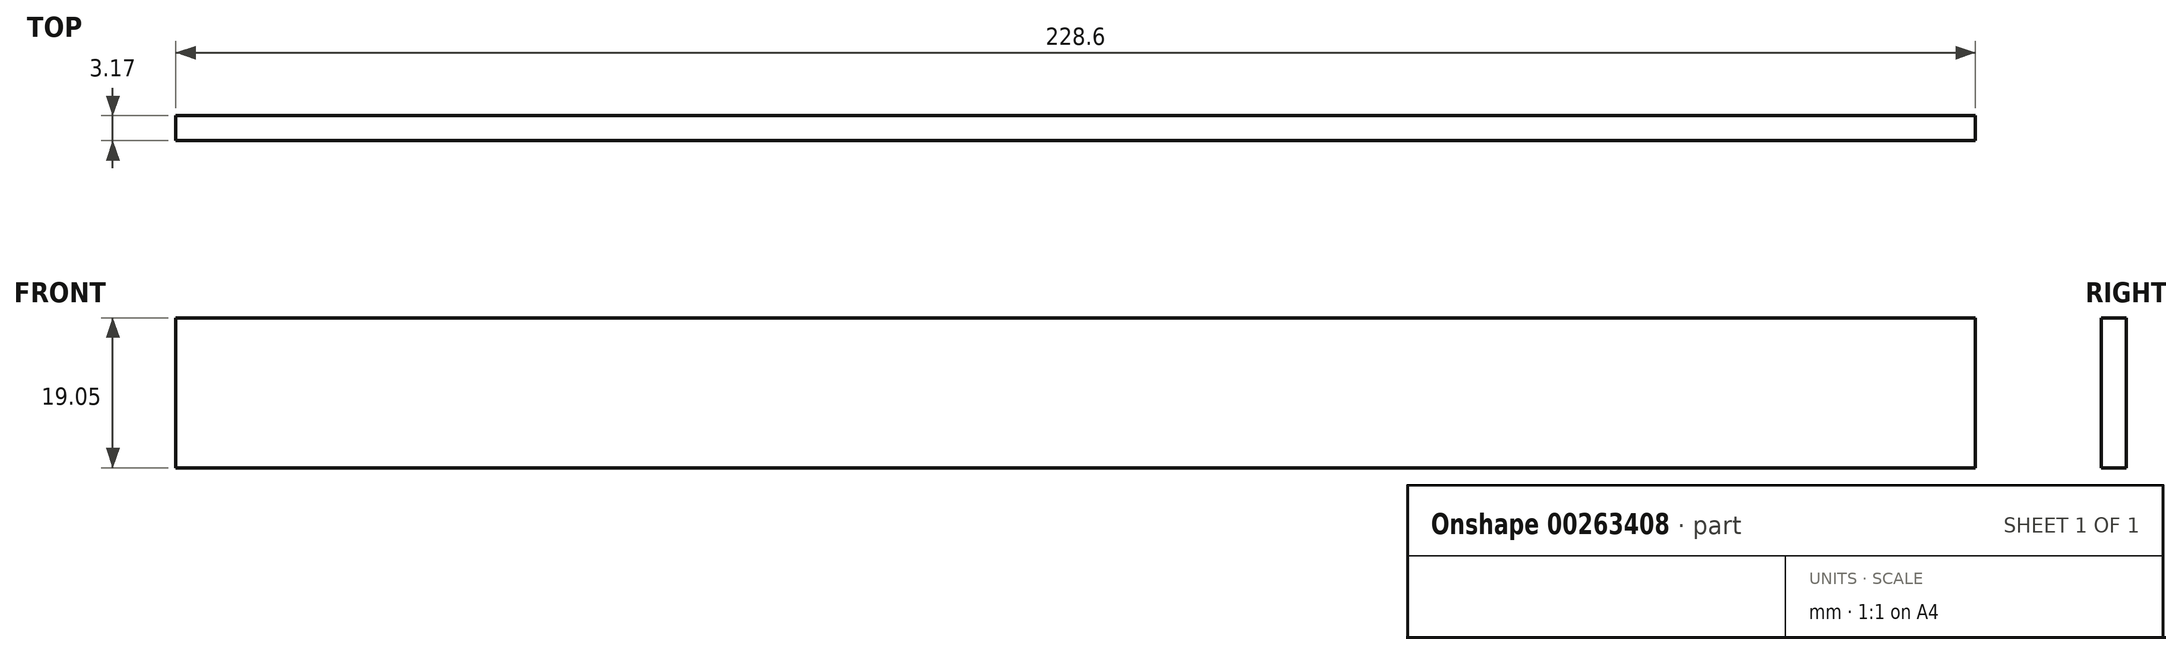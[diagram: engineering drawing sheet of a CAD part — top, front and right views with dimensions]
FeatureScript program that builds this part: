
annotation { "Feature Type Name" : "Feature", "Feature Type Description" : "" }
export const myFeature = defineFeature(function(context is Context, id is Id, definition is map)
    precondition{}
    {
        {
            var Q0;
            Q0=qCreatedBy(makeId("Front.planeOp"),FACE);
            var sketch = newSketch(context, id + "F0", { "sketchPlane" : qUnion([Q0])});
            skLineSegment(sketch, "E0.bottom", {"start": v(-188.42, 0) * mm, "end": v(40.18, 0) * mm});
            skLineSegment(sketch, "E0.top", {"start": v(-188.42, 19.05) * mm, "end": v(40.18, 19.05) * mm});
            skLineSegment(sketch, "E0.left", {"start": v(-188.42, 0) * mm, "end": v(-188.42, 19.05) * mm});
            skLineSegment(sketch, "E0.right", {"start": v(40.18, 0) * mm, "end": v(40.18, 19.05) * mm});
            skSolve(sketch);
        }
        {
            var Q0;
            Q0 = qSketchRegion(id + "F0", true);
            extrude(context, id + "F1", {"entities" : qUnion([Q0]), "depth" : 3.17 * mm});
        }
    });
